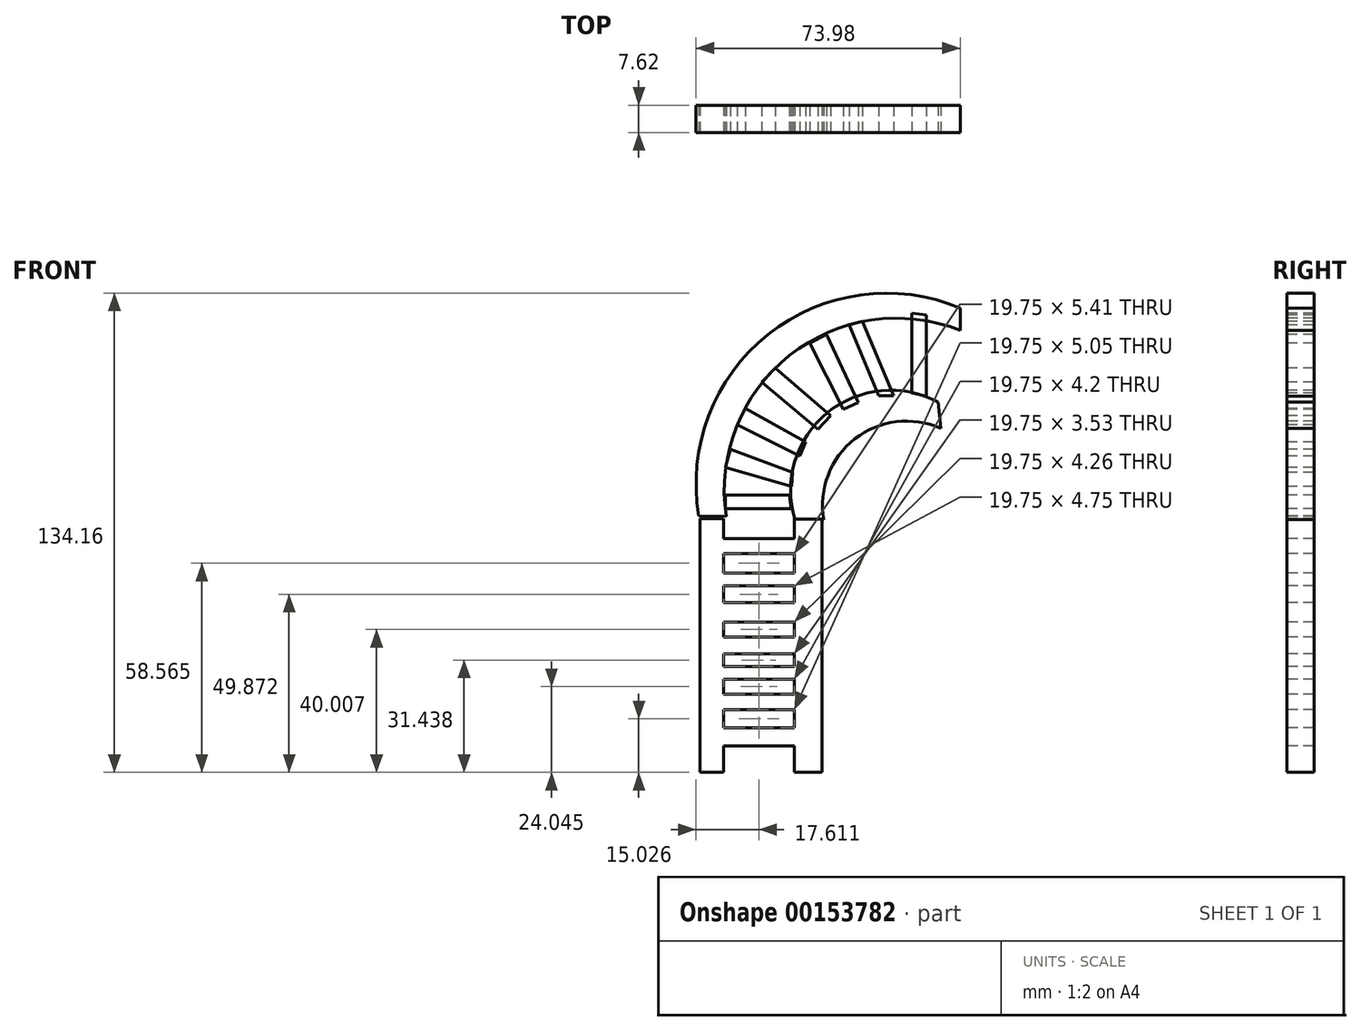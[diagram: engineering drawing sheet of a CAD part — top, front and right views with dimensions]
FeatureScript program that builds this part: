
annotation { "Feature Type Name" : "Feature", "Feature Type Description" : "" }
export const myFeature = defineFeature(function(context is Context, id is Id, definition is map)
    precondition{}
    {
        {
            var Q0;
            Q0=qCreatedBy(makeId("Front.planeOp"),FACE);
            var sketch = newSketch(context, id + "F0", { "sketchPlane" : qUnion([Q0])});
            skLineSegment(sketch, "E0", {"start": v(-72.87, 16.26) * mm, "end": v(-66.24, 16.26) * mm});
            skLineSegment(sketch, "E1", {"start": v(-66.24, 16.26) * mm, "end": v(-66.24, -54.75) * mm});
            skLineSegment(sketch, "E2", {"start": v(-66.24, -54.75) * mm, "end": v(-73.08, -54.75) * mm});
            skLineSegment(sketch, "E3", {"start": v(-72.87, 16.26) * mm, "end": v(-72.87, -54.75) * mm});
            skLineSegment(sketch, "E4", {"start": v(-46.5, 16.26) * mm, "end": v(-46.5, -54.75) * mm});
            skLineSegment(sketch, "E5", {"start": v(-46.5, -54.75) * mm, "end": v(-38.75, -54.75) * mm});
            skLineSegment(sketch, "E6", {"start": v(-38.75, -54.75) * mm, "end": v(-38.75, 16.2) * mm});
            skLineSegment(sketch, "E7", {"start": v(-46.5, 16.26) * mm, "end": v(-38.75, 16.2) * mm});
            skLineSegment(sketch, "E8", {"start": v(-66.24, 10.66) * mm, "end": v(-46.5, 10.66) * mm});
            skLineSegment(sketch, "E9", {"start": v(-66.24, 6.52) * mm, "end": v(-46.5, 6.52) * mm});
            skLineSegment(sketch, "E10", {"start": v(-66.24, 1.1) * mm, "end": v(-46.5, 1.1) * mm});
            skLineSegment(sketch, "E11", {"start": v(-66.24, -2.5) * mm, "end": v(-46.5, -2.5) * mm});
            skLineSegment(sketch, "E12", {"start": v(-66.24, -7.25) * mm, "end": v(-46.5, -7.25) * mm});
            skLineSegment(sketch, "E13", {"start": v(-66.24, -12.61) * mm, "end": v(-46.5, -12.61) * mm});
            skLineSegment(sketch, "E14", {"start": v(-66.24, -16.87) * mm, "end": v(-46.5, -16.87) * mm});
            skLineSegment(sketch, "E15", {"start": v(-66.24, -21.55) * mm, "end": v(-46.5, -21.55) * mm});
            skLineSegment(sketch, "E16", {"start": v(-66.24, -25.08) * mm, "end": v(-46.5, -25.08) * mm});
            skLineSegment(sketch, "E17", {"start": v(-66.24, -28.6) * mm, "end": v(-46.5, -28.6) * mm});
            skLineSegment(sketch, "E18", {"start": v(-66.24, -32.8) * mm, "end": v(-46.5, -32.8) * mm});
            skLineSegment(sketch, "E19", {"start": v(-66.24, -37.2) * mm, "end": v(-46.5, -37.2) * mm});
            skLineSegment(sketch, "E20", {"start": v(-66.24, -42.25) * mm, "end": v(-46.5, -42.25) * mm});
            skLineSegment(sketch, "E21", {"start": v(-66.24, -47.37) * mm, "end": v(-46.5, -47.37) * mm});
            skLineSegment(sketch, "E22", {"start": v(-46.5, -47.37) * mm, "end": v(-46.5, -51.42) * mm});
            skLineSegment(sketch, "E23", {"start": v(-46.5, -51.42) * mm, "end": v(-66.24, -51.42) * mm});
            skSolve(sketch);
        }
        {
            var Q0;
            {var subQ0=sQuery(id+"F0.wireOp",EDGE,"E8");Q0=makeQuery(id+"F0.imprint","IMPRINT",FACE,{"disambiguationData":[TD([[makeQuery(id+"F0.imprint","IMPRINT",EDGE,{"derivedFrom":subQ0}),-1.0]])]});}
            var Q1;
            {var subQ3=sQuery(id+"F0.wireOp",EDGE,"E0");Q1=makeQuery(id+"F0.imprint","IMPRINT",FACE,{"disambiguationData":[TD([[makeQuery(id+"F0.imprint","IMPRINT",EDGE,{"derivedFrom":subQ3}),-1.0]])]});}
            var Q2;
            {var subQ5=sQuery(id+"F0.wireOp",EDGE,"E5");Q2=makeQuery(id+"F0.imprint","IMPRINT",FACE,{"disambiguationData":[TD([[makeQuery(id+"F0.imprint","IMPRINT",EDGE,{"derivedFrom":subQ5}),1.0]])]});}
            var Q3;
            {var subQ0=sQuery(id+"F0.wireOp",EDGE,"E12");Q3=makeQuery(id+"F0.imprint","IMPRINT",FACE,{"disambiguationData":[TD([[makeQuery(id+"F0.imprint","IMPRINT",EDGE,{"derivedFrom":subQ0}),-1.0]])]});}
            var Q4;
            {var subQ0=sQuery(id+"F0.wireOp",EDGE,"E10");Q4=makeQuery(id+"F0.imprint","IMPRINT",FACE,{"disambiguationData":[TD([[makeQuery(id+"F0.imprint","IMPRINT",EDGE,{"derivedFrom":subQ0}),-1.0]])]});}
            var Q5;
            {var subQ0=sQuery(id+"F0.wireOp",EDGE,"E14");Q5=makeQuery(id+"F0.imprint","IMPRINT",FACE,{"disambiguationData":[TD([[makeQuery(id+"F0.imprint","IMPRINT",EDGE,{"derivedFrom":subQ0}),-1.0]])]});}
            var Q6;
            {var subQ0=sQuery(id+"F0.wireOp",EDGE,"E16");Q6=makeQuery(id+"F0.imprint","IMPRINT",FACE,{"disambiguationData":[TD([[makeQuery(id+"F0.imprint","IMPRINT",EDGE,{"derivedFrom":subQ0}),-1.0]])]});}
            var Q7;
            {var subQ0=sQuery(id+"F0.wireOp",EDGE,"E18");Q7=makeQuery(id+"F0.imprint","IMPRINT",FACE,{"disambiguationData":[TD([[makeQuery(id+"F0.imprint","IMPRINT",EDGE,{"derivedFrom":subQ0}),-1.0]])]});}
            var Q8;
            {var subQ0=sQuery(id+"F0.wireOp",EDGE,"E20");Q8=makeQuery(id+"F0.imprint","IMPRINT",FACE,{"disambiguationData":[TD([[makeQuery(id+"F0.imprint","IMPRINT",EDGE,{"derivedFrom":subQ0}),-1.0]])]});}
            extrude(context, id + "F1", {"entities" : qUnion([Q0, Q1, Q2, Q3, Q4, Q5, Q6, Q7, Q8]), "oppositeDirection" : true, "depth" : 7.62 * mm});
        }
        {
            var Q0;
            Q0=qCreatedBy(makeId("Front.planeOp"),FACE);
            var sketch = newSketch(context, id + "F2", { "sketchPlane" : qUnion([Q0])});
            skArc(sketch, "E24", {"start": v(0, 75.25) * mm, "mid": v(-53.82, 67.84) * mm, "end": v(-73.21, 17.1) * mm});
            skArc(sketch, "E25", {"start": v(-6.15, 48.9) * mm, "mid": v(-37.18, 45.96) * mm, "end": v(-46.34, 16.16) * mm});
            skLineSegment(sketch, "E26", {"start": v(0, 75.25) * mm, "end": v(0, 68.98) * mm});
            skLineSegment(sketch, "E27", {"start": v(-5.5, 41.56) * mm, "end": v(-6.15, 48.9) * mm});
            skArc(sketch, "E28", {"start": v(-5.5, 41.56) * mm, "mid": v(-29.53, 38.6) * mm, "end": v(-38.17, 15.99) * mm});
            skArc(sketch, "E29", {"start": v(0, 68.98) * mm, "mid": v(-47.84, 61.97) * mm, "end": v(-65.56, 16.98) * mm});
            skLineSegment(sketch, "E30", {"start": v(-73.84, 29.9) * mm, "end": v(-65.92, 28.23) * mm});
            skLineSegment(sketch, "E31", {"start": v(-70.23, 45.71) * mm, "end": v(-62.54, 42.35) * mm});
            skLineSegment(sketch, "E32", {"start": v(-73.21, 17.1) * mm, "end": v(-65.56, 16.98) * mm});
            skLineSegment(sketch, "E33", {"start": v(-47.5, 23.3) * mm, "end": v(-38.33, 23.3) * mm});
            skLineSegment(sketch, "E34", {"start": v(-38.17, 15.99) * mm, "end": v(-46.34, 16.16) * mm});
            skSolve(sketch);
        }
        {
            var Q0;
            {var subQ0=sQuery(id+"F2.wireOp",EDGE,"E30");Q0=makeQuery(id+"F2.imprint","IMPRINT",FACE,{"disambiguationData":[TD([[makeQuery(id+"F2.imprint","IMPRINT",EDGE,{"derivedFrom":subQ0}),1.0]])]});}
            var Q1;
            {var subQ0=sQuery(id+"F2.wireOp",EDGE,"E26");Q1=makeQuery(id+"F2.imprint","IMPRINT",FACE,{"disambiguationData":[TD([[makeQuery(id+"F2.imprint","IMPRINT",EDGE,{"derivedFrom":subQ0}),-1.0]])]});}
            var Q2;
            {var subQ2=sQuery(id+"F2.wireOp",EDGE,"E33");Q2=makeQuery(id+"F2.imprint","IMPRINT",FACE,{"disambiguationData":[TD([[makeQuery(id+"F2.imprint","IMPRINT",EDGE,{"derivedFrom":subQ2}),-1.0]])]});}
            var Q3;
            {var subQ2=sQuery(id+"F2.wireOp",EDGE,"E30");Q3=makeQuery(id+"F2.imprint","IMPRINT",FACE,{"disambiguationData":[TD([[makeQuery(id+"F2.imprint","IMPRINT",EDGE,{"derivedFrom":subQ2}),-1.0]])]});}
            var Q4;
            {var subQ0=sQuery(id+"F2.wireOp",EDGE,"E27");Q4=makeQuery(id+"F2.imprint","IMPRINT",FACE,{"disambiguationData":[TD([[makeQuery(id+"F2.imprint","IMPRINT",EDGE,{"derivedFrom":subQ0}),1.0]])]});}
            extrude(context, id + "F3", {"entities" : qUnion([Q0, Q1, Q2, Q3, Q4]), "oppositeDirection" : true, "depth" : 7.62 * mm});
        }
        {
            var Q0;
            Q0=qCreatedBy(makeId("Front.planeOp"),FACE);
            var sketch = newSketch(context, id + "F4", { "sketchPlane" : qUnion([Q0])});
            skLineSegment(sketch, "E35", {"start": v(-65.74, 22.9) * mm, "end": v(-47.8, 22.9) * mm});
            skLineSegment(sketch, "E36", {"start": v(-47.33, 19.08) * mm, "end": v(-65.74, 19.08) * mm});
            skLineSegment(sketch, "E37", {"start": v(-64.31, 35.75) * mm, "end": v(-47.01, 29.24) * mm});
            skLineSegment(sketch, "E38", {"start": v(-65.74, 30.67) * mm, "end": v(-47.17, 25.27) * mm});
            skLineSegment(sketch, "E39", {"start": v(-62.41, 42.57) * mm, "end": v(-44.95, 33.84) * mm});
            skLineSegment(sketch, "E40", {"start": v(-60.23, 47.13) * mm, "end": v(-43.25, 37.79) * mm});
            skLineSegment(sketch, "E41", {"start": v(-13.53, 73.78) * mm, "end": v(-13.53, 51.49) * mm});
            skLineSegment(sketch, "E42", {"start": v(-9.46, 50.61) * mm, "end": v(-9.46, 73.36) * mm});
            skLineSegment(sketch, "E43", {"start": v(-18.66, 50.66) * mm, "end": v(-27.39, 71.54) * mm});
            skLineSegment(sketch, "E44", {"start": v(-22.82, 50.66) * mm, "end": v(-31.14, 70.53) * mm});
            skLineSegment(sketch, "E45", {"start": v(-42.1, 65.43) * mm, "end": v(-32.73, 46.86) * mm});
            skLineSegment(sketch, "E46", {"start": v(-37.4, 67.88) * mm, "end": v(-28.6, 48.76) * mm});
            skLineSegment(sketch, "E47", {"start": v(-51.74, 58.42) * mm, "end": v(-36.26, 45.09) * mm});
            skLineSegment(sketch, "E48", {"start": v(-55.59, 54.48) * mm, "end": v(-39.87, 41.3) * mm});
            skLineSegment(sketch, "E49", {"start": v(-65.74, 19.08) * mm, "end": v(-65.74, 22.9) * mm});
            skLineSegment(sketch, "E50", {"start": v(-47.8, 22.9) * mm, "end": v(-47.33, 19.08) * mm});
            skLineSegment(sketch, "E51", {"start": v(-65.74, 30.67) * mm, "end": v(-64.31, 35.75) * mm});
            skLineSegment(sketch, "E52", {"start": v(-47.17, 25.27) * mm, "end": v(-47.01, 29.24) * mm});
            skLineSegment(sketch, "E53", {"start": v(-44.95, 33.84) * mm, "end": v(-43.25, 37.79) * mm});
            skLineSegment(sketch, "E54", {"start": v(-62.41, 42.57) * mm, "end": v(-60.23, 47.13) * mm});
            skLineSegment(sketch, "E55", {"start": v(-55.59, 54.48) * mm, "end": v(-51.74, 58.42) * mm});
            skLineSegment(sketch, "E56", {"start": v(-39.87, 41.3) * mm, "end": v(-36.26, 45.09) * mm});
            skLineSegment(sketch, "E57", {"start": v(-32.73, 46.86) * mm, "end": v(-28.6, 48.76) * mm});
            skLineSegment(sketch, "E58", {"start": v(-42.1, 65.43) * mm, "end": v(-37.4, 67.88) * mm});
            skLineSegment(sketch, "E59", {"start": v(-31.14, 70.53) * mm, "end": v(-27.39, 71.54) * mm});
            skLineSegment(sketch, "E60", {"start": v(-22.82, 50.66) * mm, "end": v(-18.66, 50.66) * mm});
            skLineSegment(sketch, "E61", {"start": v(-13.53, 51.49) * mm, "end": v(-9.46, 50.61) * mm});
            skLineSegment(sketch, "E62", {"start": v(-13.53, 73.78) * mm, "end": v(-9.46, 73.36) * mm});
            skSolve(sketch);
        }
        {
            var Q0;
            Q0 = qSketchRegion(id + "F4", true);
            extrude(context, id + "F5", {"entities" : qUnion([Q0]), "oppositeDirection" : true, "depth" : 7.56 * mm});
        }
    });
